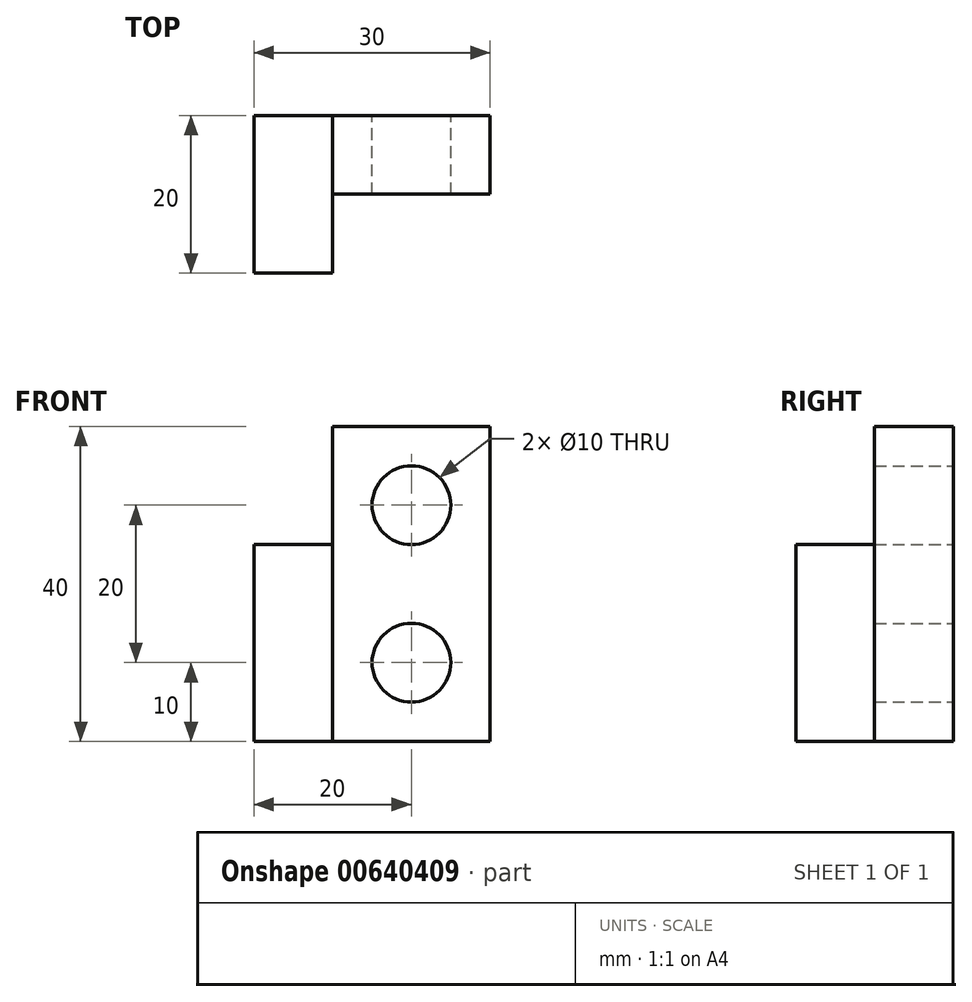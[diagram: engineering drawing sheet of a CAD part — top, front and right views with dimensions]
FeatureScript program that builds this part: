
annotation { "Feature Type Name" : "Feature", "Feature Type Description" : "" }
export const myFeature = defineFeature(function(context is Context, id is Id, definition is map)
    precondition{}
    {
        {
            var Q0;
            Q0=qCreatedBy(makeId("Front.planeOp"),FACE);
            var sketch = newSketch(context, id + "F0", { "sketchPlane" : qUnion([Q0])});
            skLineSegment(sketch, "E0.bottom", {"start": v(10, 20) * mm, "end": v(-10, 20) * mm});
            skLineSegment(sketch, "E0.top", {"start": v(10, -20) * mm, "end": v(-10, -20) * mm});
            skLineSegment(sketch, "E0.left", {"start": v(10, 20) * mm, "end": v(10, -20) * mm});
            skLineSegment(sketch, "E0.right", {"start": v(-10, 20) * mm, "end": v(-10, -20) * mm});
            skPoint(sketch, "E0.middle", {"position": v(0, 0) * mm});
            skLineSegment(sketch, "E1.bottom", {"start": v(-10, -20) * mm, "end": v(-20, -20) * mm});
            skLineSegment(sketch, "E1.top", {"start": v(-10, 5) * mm, "end": v(-20, 5) * mm});
            skLineSegment(sketch, "E1.left", {"start": v(-10, -20) * mm, "end": v(-10, 5) * mm});
            skLineSegment(sketch, "E1.right", {"start": v(-20, -20) * mm, "end": v(-20, 5) * mm});
            skCircle(sketch, "E2", {"center": v(0, -10) * mm, "radius": 5 * mm});
            skCircle(sketch, "E3", {"center": v(0, 10) * mm, "radius": 5 * mm});
            skSolve(sketch);
        }
        {
            var Q0;
            Q0=makeQuery(id+"F0.imprint","IMPRINT",FACE,{"disambiguationData":[TD([[makeQuery(id+"F0.imprint","IMPRINT",EDGE,{"derivedFrom":sQuery(id+"F0.wireOp",EDGE,"E0.bottom")}),1.0]])]});
            extrude(context, id + "F1", {"entities" : qUnion([Q0]), "depth" : 15 * mm, "offsetDistance" : 25 * mm});
        }
        {
            var Q0;
            Q0 = qSketchRegion(id + "F0", true);
            var Q1;
            Q1=makeQuery(id+"F1.opExtrude","CAP_FACE",FACE,{"disambiguationData":[OSD([sQuery(id+"F0.wireOp",EDGE,"E0.bottom"),sQuery(id+"F0.wireOp",EDGE,"E0.top"),sQuery(id+"F0.wireOp",EDGE,"E0.left"),sQuery(id+"F0.wireOp",EDGE,"E0.right"),sQuery(id+"F0.wireOp",EDGE,"E1.left"),sQuery(id+"F0.wireOp",EDGE,"E2"),sQuery(id+"F0.wireOp",EDGE,"E3")])],"isStart":false});
            extrude(context, id + "F2", {"entities" : qUnion([Q0, Q1]), "operationType" : NewBodyOperationType.ADD, "depth" : 20 * mm, "offsetDistance" : 25 * mm});
        }
        {
            var Q0;
            Q0=makeQuery(id+"F2.opExtrude","CAP_FACE",FACE,{"disambiguationData":[OSD([sQuery(id+"F0.wireOp",EDGE,"E0.bottom"),sQuery(id+"F0.wireOp",EDGE,"E0.top"),sQuery(id+"F0.wireOp",EDGE,"E0.left"),sQuery(id+"F0.wireOp",EDGE,"E0.right"),sQuery(id+"F0.wireOp",EDGE,"E1.left"),sQuery(id+"F0.wireOp",EDGE,"E2"),sQuery(id+"F0.wireOp",EDGE,"E3")])],"isStart":false});
            extrude(context, id + "F3", {"entities" : qUnion([Q0]), "operationType" : NewBodyOperationType.REMOVE, "oppositeDirection" : true, "depth" : 25 * mm, "offsetDistance" : 25 * mm});
        }
    });
